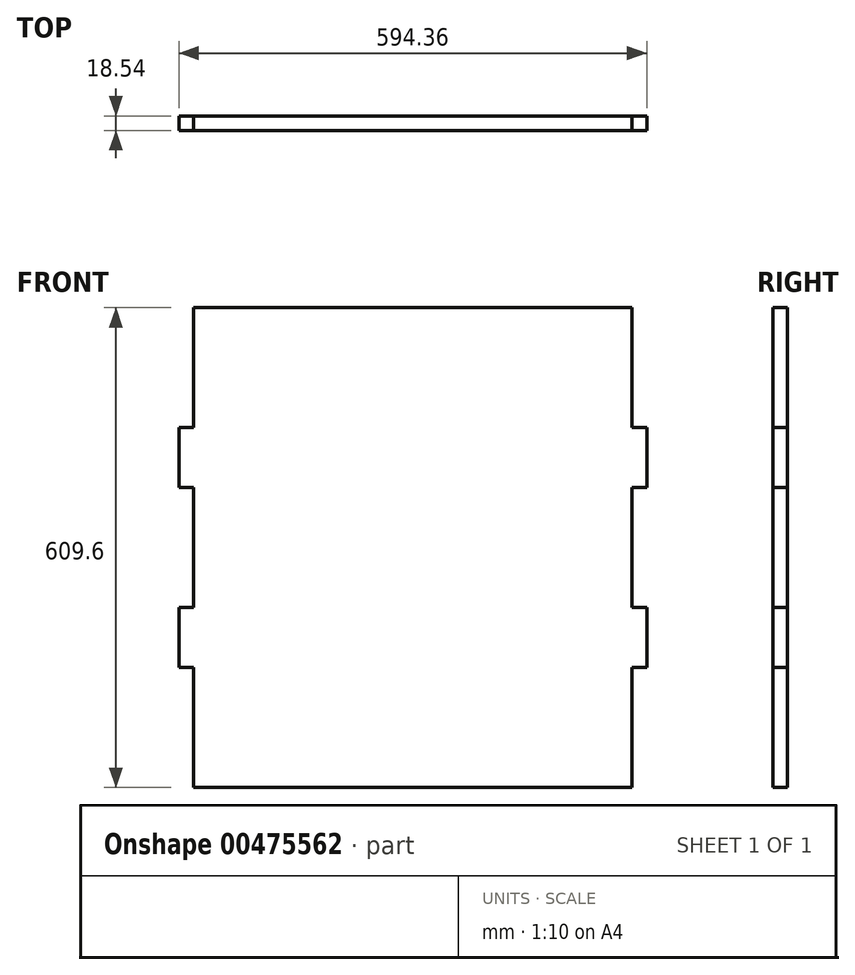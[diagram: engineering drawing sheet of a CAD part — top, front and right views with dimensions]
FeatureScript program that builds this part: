
annotation { "Feature Type Name" : "Feature", "Feature Type Description" : "" }
export const myFeature = defineFeature(function(context is Context, id is Id, definition is map)
    precondition{}
    {
        {
            var Q0;
            Q0=qCreatedBy(makeId("Front.planeOp"),FACE);
            var sketch = newSketch(context, id + "F0", { "sketchPlane" : qUnion([Q0])});
            skLineSegment(sketch, "E0.bottom", {"start": v(-569.02, 457.2) * mm, "end": v(-11.74, 457.2) * mm});
            skLineSegment(sketch, "E0.top", {"start": v(-569.02, -152.4) * mm, "end": v(-11.74, -152.4) * mm});
            skLineSegment(sketch, "E0.left", {"start": v(-569.02, 457.2) * mm, "end": v(-569.02, -152.4) * mm});
            skLineSegment(sketch, "E0.right", {"start": v(-11.74, 457.2) * mm, "end": v(-11.74, -152.4) * mm});
            skLineSegment(sketch, "E1.bottom", {"start": v(-11.74, 228.6) * mm, "end": v(6.8, 228.6) * mm});
            skLineSegment(sketch, "E1.top", {"start": v(-11.74, 304.8) * mm, "end": v(6.8, 304.8) * mm});
            skLineSegment(sketch, "E1.left", {"start": v(-11.74, 304.8) * mm, "end": v(-11.74, 228.6) * mm});
            skLineSegment(sketch, "E1.right", {"start": v(6.8, 304.8) * mm, "end": v(6.8, 228.6) * mm});
            skLineSegment(sketch, "E2.bottom", {"start": v(-569.02, 304.8) * mm, "end": v(-587.56, 304.8) * mm});
            skLineSegment(sketch, "E2.top", {"start": v(-569.02, 228.6) * mm, "end": v(-587.56, 228.6) * mm});
            skLineSegment(sketch, "E2.left", {"start": v(-569.02, 304.8) * mm, "end": v(-569.02, 228.6) * mm});
            skLineSegment(sketch, "E2.right", {"start": v(-587.56, 304.8) * mm, "end": v(-587.56, 228.6) * mm});
            skLineSegment(sketch, "E3.bottom", {"start": v(-569.02, 76.2) * mm, "end": v(-587.56, 76.2) * mm});
            skLineSegment(sketch, "E3.top", {"start": v(-569.02, 0) * mm, "end": v(-587.56, 0) * mm});
            skLineSegment(sketch, "E3.left", {"start": v(-569.02, 76.2) * mm, "end": v(-569.02, 0) * mm});
            skLineSegment(sketch, "E3.right", {"start": v(-587.56, 76.2) * mm, "end": v(-587.56, 0) * mm});
            skLineSegment(sketch, "E4.bottom", {"start": v(-11.74, 76.2) * mm, "end": v(6.8, 76.2) * mm});
            skLineSegment(sketch, "E4.top", {"start": v(-11.74, 0) * mm, "end": v(6.8, 0) * mm});
            skLineSegment(sketch, "E4.left", {"start": v(-11.74, 76.2) * mm, "end": v(-11.74, 0) * mm});
            skLineSegment(sketch, "E4.right", {"start": v(6.8, 76.2) * mm, "end": v(6.8, 0) * mm});
            skSolve(sketch);
        }
        {
            var Q0;
            {var subQ4=sQuery(id+"F0.wireOp",EDGE,"E0.bottom");Q0=makeQuery(id+"F0.imprint","IMPRINT",FACE,{"disambiguationData":[TD([[makeQuery(id+"F0.imprint","IMPRINT",EDGE,{"derivedFrom":subQ4}),-1.0]])]});}
            var Q1;
            Q1=makeQuery(id+"F0.imprint","IMPRINT",FACE,{"disambiguationData":[TD([[makeQuery(id+"F0.imprint","IMPRINT",EDGE,{"derivedFrom":sQuery(id+"F0.wireOp",EDGE,"E2.bottom")}),1.0]])]});
            var Q2;
            Q2=makeQuery(id+"F0.imprint","IMPRINT",FACE,{"disambiguationData":[TD([[makeQuery(id+"F0.imprint","IMPRINT",EDGE,{"derivedFrom":sQuery(id+"F0.wireOp",EDGE,"E3.bottom")}),1.0]])]});
            var Q3;
            Q3=makeQuery(id+"F0.imprint","IMPRINT",FACE,{"disambiguationData":[TD([[makeQuery(id+"F0.imprint","IMPRINT",EDGE,{"derivedFrom":sQuery(id+"F0.wireOp",EDGE,"E1.bottom")}),1.0]])]});
            var Q4;
            Q4=makeQuery(id+"F0.imprint","IMPRINT",FACE,{"disambiguationData":[TD([[makeQuery(id+"F0.imprint","IMPRINT",EDGE,{"derivedFrom":sQuery(id+"F0.wireOp",EDGE,"E4.bottom")}),-1.0]])]});
            extrude(context, id + "F1", {"entities" : qUnion([Q0, Q1, Q2, Q3, Q4]), "depth" : 18.54 * mm, "offsetDistance" : 25.4 * mm});
        }
    });
